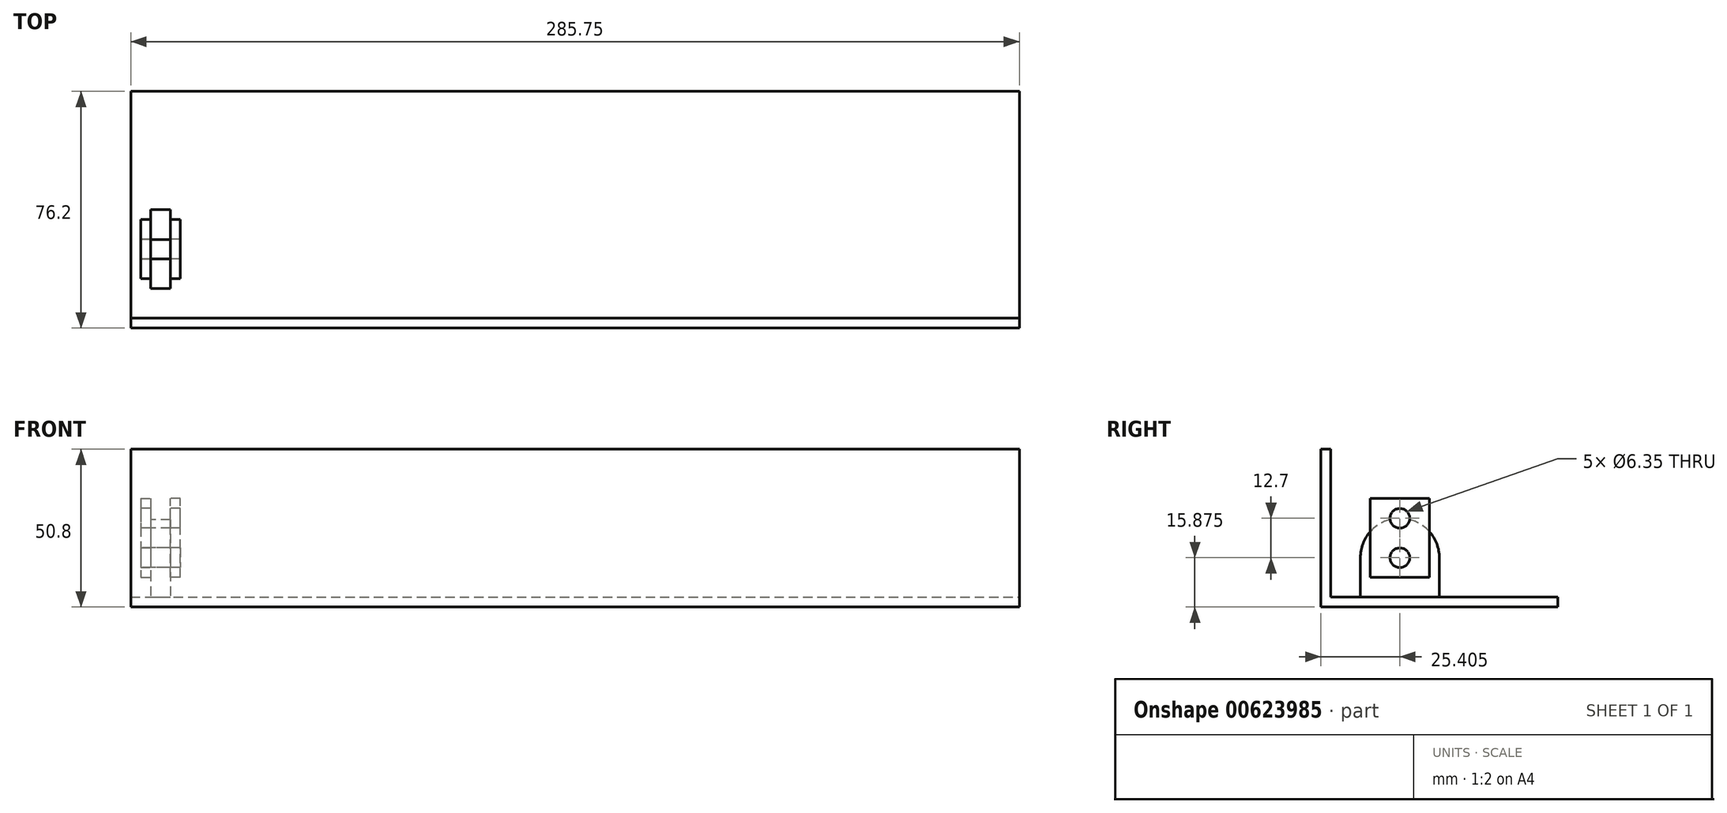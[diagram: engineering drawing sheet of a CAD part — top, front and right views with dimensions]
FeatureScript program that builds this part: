
annotation { "Feature Type Name" : "Feature", "Feature Type Description" : "" }
export const myFeature = defineFeature(function(context is Context, id is Id, definition is map)
    precondition{}
    {
        {
            var Q0;
            Q0=qCreatedBy(makeId("Top.planeOp"),FACE);
            var sketch = newSketch(context, id + "F0", { "sketchPlane" : qUnion([Q0])});
            skLineSegment(sketch, "E0.bottom", {"start": v(-137.7, 40.98) * mm, "end": v(148.04, 40.98) * mm});
            skLineSegment(sketch, "E0.top", {"start": v(-137.7, -35.22) * mm, "end": v(148.04, -35.22) * mm});
            skLineSegment(sketch, "E0.left", {"start": v(-137.7, 40.98) * mm, "end": v(-137.7, -35.22) * mm});
            skLineSegment(sketch, "E0.right", {"start": v(148.04, 40.98) * mm, "end": v(148.04, -35.22) * mm});
            skSolve(sketch);
        }
        {
            var Q0;
            Q0=makeQuery(id+"F0.imprint","IMPRINT",FACE,{"disambiguationData":[TD([[makeQuery(id+"F0.imprint","IMPRINT",EDGE,{"derivedFrom":sQuery(id+"F0.wireOp",EDGE,"E0.bottom")}),-1.0]])]});
            extrude(context, id + "F1", {"entities" : qUnion([Q0]), "depth" : 3.17 * mm, "offsetDistance" : 25.4 * mm});
        }
        {
            var Q0;
            Q0=makeQuery(id+"F1.opExtrude","CAP_FACE",FACE,{"disambiguationData":[OSD([sQuery(id+"F0.wireOp",EDGE,"E0.bottom"),sQuery(id+"F0.wireOp",EDGE,"E0.top"),sQuery(id+"F0.wireOp",EDGE,"E0.left"),sQuery(id+"F0.wireOp",EDGE,"E0.right")])],"isStart":false});
            var sketch = newSketch(context, id + "F2", { "sketchPlane" : qUnion([Q0])});
            skLineSegment(sketch, "E1.bottom", {"start": v(-137.7, -35.22) * mm, "end": v(148.04, -35.22) * mm});
            skLineSegment(sketch, "E1.top", {"start": v(-137.7, -32.04) * mm, "end": v(148.04, -32.04) * mm});
            skLineSegment(sketch, "E1.left", {"start": v(-137.7, -35.22) * mm, "end": v(-137.7, -32.04) * mm});
            skLineSegment(sketch, "E1.right", {"start": v(148.04, -35.22) * mm, "end": v(148.04, -32.04) * mm});
            skSolve(sketch);
        }
        {
            var Q0;
            Q0=makeQuery(id+"F2.imprint","IMPRINT",FACE,{"disambiguationData":[TD([[makeQuery(id+"F2.imprint","IMPRINT",EDGE,{"derivedFrom":sQuery(id+"F2.wireOp",EDGE,"E1.bottom")}),1.0]])]});
            extrude(context, id + "F3", {"entities" : qUnion([Q0]), "operationType" : NewBodyOperationType.ADD, "depth" : 47.62 * mm, "offsetDistance" : 25.4 * mm});
        }
        {
            var Q0;
            Q0=makeQuery(id+"F1.opExtrude","CAP_FACE",FACE,{"disambiguationData":[OSD([sQuery(id+"F0.wireOp",EDGE,"E0.bottom"),sQuery(id+"F0.wireOp",EDGE,"E0.top"),sQuery(id+"F0.wireOp",EDGE,"E0.left"),sQuery(id+"F0.wireOp",EDGE,"E0.right")])],"isStart":false});
            var sketch = newSketch(context, id + "F4", { "sketchPlane" : qUnion([Q0])});
            skLineSegment(sketch, "E2.bottom", {"start": v(-131.36, 2.88) * mm, "end": v(-125, 2.88) * mm});
            skLineSegment(sketch, "E2.top", {"start": v(-131.36, -22.52) * mm, "end": v(-125, -22.52) * mm});
            skLineSegment(sketch, "E2.left", {"start": v(-131.36, 2.88) * mm, "end": v(-131.36, -22.52) * mm});
            skLineSegment(sketch, "E2.right", {"start": v(-125, 2.88) * mm, "end": v(-125, -22.52) * mm});
            skSolve(sketch);
        }
        {
            var Q0;
            Q0=makeQuery(id+"F4.imprint","IMPRINT",FACE,{"disambiguationData":[TD([[makeQuery(id+"F4.imprint","IMPRINT",EDGE,{"derivedFrom":sQuery(id+"F4.wireOp",EDGE,"E2.bottom")}),-1.0]])]});
            extrude(context, id + "F5", {"entities" : qUnion([Q0]), "operationType" : NewBodyOperationType.ADD, "depth" : 25.4 * mm, "offsetDistance" : 25.4 * mm});
        }
        {
            var Q0;
            Q0=makeQuery(id+"F5.opExtrude","CAP_EDGE",EDGE,{"disambiguationData":[OSD([sQuery(id+"F4.wireOp",EDGE,"E2.bottom")])],"isStart":false});
            var Q1;
            Q1=makeQuery(id+"F5.opExtrude","CAP_EDGE",EDGE,{"disambiguationData":[OSD([sQuery(id+"F4.wireOp",EDGE,"E2.top")])],"isStart":false});
            fillet(context, id + "F6", {"entities" : qUnion([Q0, Q1]), "radius" : 12.7 * mm, "tangentPropagation" : true, "allowEdgeOverflow" : false});
        }
        {
            var Q0;
            Q0=makeQuery(id+"F5.opExtrude","SWEPT_FACE",FACE,{"disambiguationData":[OSD([sQuery(id+"F4.wireOp",EDGE,"E2.left")])]});
            var sketch = newSketch(context, id + "F7", { "sketchPlane" : qUnion([Q0])});
            skCircle(sketch, "E3", {"center": v(9.82, 15.88) * mm, "radius": 3.18 * mm});
            skSolve(sketch);
        }
        {
            var Q0;
            Q0=makeQuery(id+"F7.imprint","IMPRINT",FACE,{"disambiguationData":[TD([[makeQuery(id+"F7.imprint","IMPRINT",EDGE,{"derivedFrom":sQuery(id+"F7.wireOp",EDGE,"E3")}),1.0]])]});
            extrude(context, id + "F8", {"entities" : qUnion([Q0]), "operationType" : NewBodyOperationType.REMOVE, "oppositeDirection" : true, "depth" : 6.35 * mm, "offsetDistance" : 25.4 * mm});
        }
        {
            var Q0;
            Q0=makeQuery(id+"F5.opExtrude","SWEPT_FACE",FACE,{"disambiguationData":[OSD([sQuery(id+"F4.wireOp",EDGE,"E2.right")])]});
            var sketch = newSketch(context, id + "F9", { "sketchPlane" : qUnion([Q0])});
            skLineSegment(sketch, "E4.bottom", {"start": v(-19.34, 9.53) * mm, "end": v(-0.3, 9.53) * mm});
            skLineSegment(sketch, "E4.top", {"start": v(-19.34, 34.93) * mm, "end": v(-0.3, 34.93) * mm});
            skLineSegment(sketch, "E4.left", {"start": v(-19.34, 9.52) * mm, "end": v(-19.34, 34.93) * mm});
            skLineSegment(sketch, "E4.right", {"start": v(-0.3, 9.53) * mm, "end": v(-0.3, 34.93) * mm});
            skSolve(sketch);
        }
        {
            var Q0;
            {var subQ0=sQuery(id+"F9.wireOp",EDGE,"E4.top");Q0=makeQuery(id+"F9.imprint","IMPRINT",FACE,{"disambiguationData":[TD([[makeQuery(id+"F9.imprint","IMPRINT",EDGE,{"derivedFrom":subQ0}),-1.0]])]});}
            var Q1;
            {var subQ1=sQuery(id+"F9.wireOp",EDGE,"E4.bottom");Q1=makeQuery(id+"F9.imprint","IMPRINT",FACE,{"disambiguationData":[TD([[makeQuery(id+"F9.imprint","IMPRINT",EDGE,{"derivedFrom":subQ1}),1.0]])]});}
            extrude(context, id + "F10", {"entities" : qUnion([Q0, Q1]), "depth" : 3.17 * mm, "offsetDistance" : 25.4 * mm});
        }
        {
            var Q0;
            Q0=makeQuery(id+"F5.opExtrude","SWEPT_FACE",FACE,{"disambiguationData":[OSD([sQuery(id+"F4.wireOp",EDGE,"E2.left")])]});
            var sketch = newSketch(context, id + "F11", { "sketchPlane" : qUnion([Q0])});
            skLineSegment(sketch, "E5.bottom", {"start": v(0.3, 34.93) * mm, "end": v(19.34, 34.93) * mm});
            skLineSegment(sketch, "E5.top", {"start": v(0.3, 9.52) * mm, "end": v(19.34, 9.53) * mm});
            skLineSegment(sketch, "E5.left", {"start": v(0.3, 34.93) * mm, "end": v(0.3, 9.52) * mm});
            skLineSegment(sketch, "E5.right", {"start": v(19.34, 34.93) * mm, "end": v(19.34, 9.52) * mm});
            skSolve(sketch);
        }
        {
            var Q0;
            {var subQ1=sQuery(id+"F11.wireOp",EDGE,"E5.top");Q0=makeQuery(id+"F11.imprint","IMPRINT",FACE,{"disambiguationData":[TD([[makeQuery(id+"F11.imprint","IMPRINT",EDGE,{"derivedFrom":subQ1}),1.0]])]});}
            var Q1;
            {var subQ0=sQuery(id+"F11.wireOp",EDGE,"E5.bottom");Q1=makeQuery(id+"F11.imprint","IMPRINT",FACE,{"disambiguationData":[TD([[makeQuery(id+"F11.imprint","IMPRINT",EDGE,{"derivedFrom":subQ0}),-1.0]])]});}
            extrude(context, id + "F12", {"entities" : qUnion([Q0, Q1]), "depth" : 3.17 * mm, "offsetDistance" : 25.4 * mm});
        }
        {
            var Q0;
            Q0=makeQuery(id+"F12.opExtrude","CAP_FACE",FACE,{"disambiguationData":[OSD([sQuery(id+"F7.wireOp",EDGE,"E3"),sQuery(id+"F11.wireOp",EDGE,"E5.bottom"),sQuery(id+"F11.wireOp",EDGE,"E5.top"),sQuery(id+"F11.wireOp",EDGE,"E5.left"),sQuery(id+"F11.wireOp",EDGE,"E5.right")])],"isStart":false});
            var sketch = newSketch(context, id + "F13", { "sketchPlane" : qUnion([Q0])});
            skCircle(sketch, "E6", {"center": v(9.82, 28.58) * mm, "radius": 3.18 * mm});
            skPoint(sketch, "E6.centerSnap0", {"position": v(9.82, 34.93) * mm});
            skSolve(sketch);
        }
        {
            var Q0;
            Q0=makeQuery(id+"F13.imprint","IMPRINT",FACE,{"disambiguationData":[TD([[makeQuery(id+"F13.imprint","IMPRINT",EDGE,{"derivedFrom":sQuery(id+"F13.wireOp",EDGE,"E6")}),1.0]])]});
            extrude(context, id + "F14", {"entities" : qUnion([Q0]), "operationType" : NewBodyOperationType.REMOVE, "oppositeDirection" : true, "depth" : 25.4 * mm, "offsetDistance" : 25.4 * mm});
        }
        {
            var Q0;
            Q0=makeQuery(id+"F10.opExtrude","CAP_FACE",FACE,{"disambiguationData":[OSD([sQuery(id+"F7.wireOp",EDGE,"E3"),sQuery(id+"F9.wireOp",EDGE,"E4.bottom"),sQuery(id+"F9.wireOp",EDGE,"E4.top"),sQuery(id+"F9.wireOp",EDGE,"E4.left"),sQuery(id+"F9.wireOp",EDGE,"E4.right")])],"isStart":false});
            var sketch = newSketch(context, id + "F15", { "sketchPlane" : qUnion([Q0])});
            skCircle(sketch, "E7", {"center": v(-9.82, 28.58) * mm, "radius": 3.18 * mm});
            skPoint(sketch, "E7.centerSnap0", {"position": v(-9.82, 34.93) * mm});
            skSolve(sketch);
        }
        {
            var Q0;
            Q0=makeQuery(id+"F15.imprint","IMPRINT",FACE,{"disambiguationData":[TD([[makeQuery(id+"F15.imprint","IMPRINT",EDGE,{"derivedFrom":sQuery(id+"F15.wireOp",EDGE,"E7")}),1.0]])]});
            extrude(context, id + "F16", {"entities" : qUnion([Q0]), "operationType" : NewBodyOperationType.REMOVE, "oppositeDirection" : true, "depth" : 25.4 * mm, "offsetDistance" : 25.4 * mm});
        }
        {
            var Q0;
            Q0=makeQuery(id+"F12.opExtrude","CAP_FACE",FACE,{"disambiguationData":[OSD([sQuery(id+"F7.wireOp",EDGE,"E3"),sQuery(id+"F11.wireOp",EDGE,"E5.bottom"),sQuery(id+"F11.wireOp",EDGE,"E5.top"),sQuery(id+"F11.wireOp",EDGE,"E5.left"),sQuery(id+"F11.wireOp",EDGE,"E5.right")])],"isStart":false});
            var sketch = newSketch(context, id + "F17", { "sketchPlane" : qUnion([Q0])});
            skCircle(sketch, "E8", {"center": v(9.82, 15.88) * mm, "radius": 3.18 * mm});
            skSolve(sketch);
        }
        {
            var Q0;
            Q0=makeQuery(id+"F17.imprint","IMPRINT",FACE,{"disambiguationData":[TD([[makeQuery(id+"F17.imprint","IMPRINT",EDGE,{"derivedFrom":sQuery(id+"F17.wireOp",EDGE,"E8")}),1.0]])]});
            extrude(context, id + "F18", {"entities" : qUnion([Q0]), "oppositeDirection" : true, "depth" : 12.7 * mm, "offsetDistance" : 25.4 * mm});
        }
        {
            var Q0;
            Q0=makeQuery(id+"F5.opExtrude","SWEPT_FACE",FACE,{"disambiguationData":[OSD([sQuery(id+"F4.wireOp",EDGE,"E2.left")])]});
            var sketch = newSketch(context, id + "F19", { "sketchPlane" : qUnion([Q0])});
            skCircle(sketch, "E9", {"center": v(9.82, 28.58) * mm, "radius": 3.17 * mm});
            skSolve(sketch);
        }
        {
            var Q0;
            {var subQ0=sQuery(id+"F19.wireOp",EDGE,"E9");var subQ1=makeQuery(id+"F6.opFillet","BLEND_EDGE",EDGE,{"blendedFrom":[makeQuery(id+"F5.opExtrude","CAP_EDGE",EDGE,{"disambiguationData":[OSD([sQuery(id+"F4.wireOp",EDGE,"E2.bottom")])],"isStart":false}),makeQuery(id+"F5.opExtrude","SWEPT_FACE",FACE,{"disambiguationData":[OSD([sQuery(id+"F4.wireOp",EDGE,"E2.left")])]})],"blendedInto":[makeQuery(id+"F5.opExtrude","SWEPT_FACE",FACE,{"disambiguationData":[OSD([sQuery(id+"F4.wireOp",EDGE,"E2.left")])]})]});var subQ2=makeQuery(id+"F19.imprint","INTERSECT",VERTEX,{"disambiguationData":[OD(0.0)],"derivedFrom":[subQ1,subQ0]});Q0=makeQuery(id+"F19.imprint","IMPRINT",FACE,{"disambiguationData":[TD([[makeQuery(id+"F19.imprint","IMPRINT",EDGE,{"disambiguationData":[TD([[subQ2,-1.0]])],"derivedFrom":subQ0}),1.0]])]});}
            extrude(context, id + "F20", {"entities" : qUnion([Q0]), "operationType" : NewBodyOperationType.REMOVE, "oppositeDirection" : true, "depth" : 6.35 * mm, "offsetDistance" : 25.4 * mm});
        }
    });
